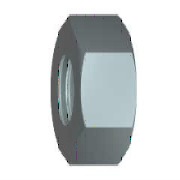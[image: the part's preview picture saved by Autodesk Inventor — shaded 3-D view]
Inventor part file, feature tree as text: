
AUTODESK INVENTOR PART (.ipt)
format: ipt  version: 2023 (Build 270158000, 158)  size: 177,152 bytes
history: native  units: mm
features: sketch x5, plane x2, mirror x1, projected_geometry x1
ambient origin geometry x8: Origin, YZ Plane, XZ Plane, XY Plane, X Axis, Y Axis, Z Axis, Center Point
bodies: Solid1 (feature_tree)
feature tree (9):
  plane  "Work Plane1"
  plane  "Work Plane2"
  mirror  "Симметричное отображение1"
  sketch  "Sketch1"  dims[d1=9.5mm]
  sketch  "Sketch4"  dims[d12=14.5mm]
  sketch  "Sketch2"  dims[d2=0.0mm]
  sketch  "Sketch5"  dims[d13=24.5mm d14=90.0deg d15=0.95mm d38=8.376mm d39=6.0mm d40=4.0mm d41=2.0mm d42=90.0deg d43=8.0mm d44=20.594885mm d54=45.0deg d55=10.0mm d56=90.0deg d57=45.0deg d58=10.0mm d59=90.0deg d60=9.5mm d63=0.0mm d64=0.0mm d65=0.0mm d66=0.0mm d67=17.0mm]
  projected_geometry  "Projected Loop1"
  sketch  "Sketch3"  dims[d11=30.0deg]
